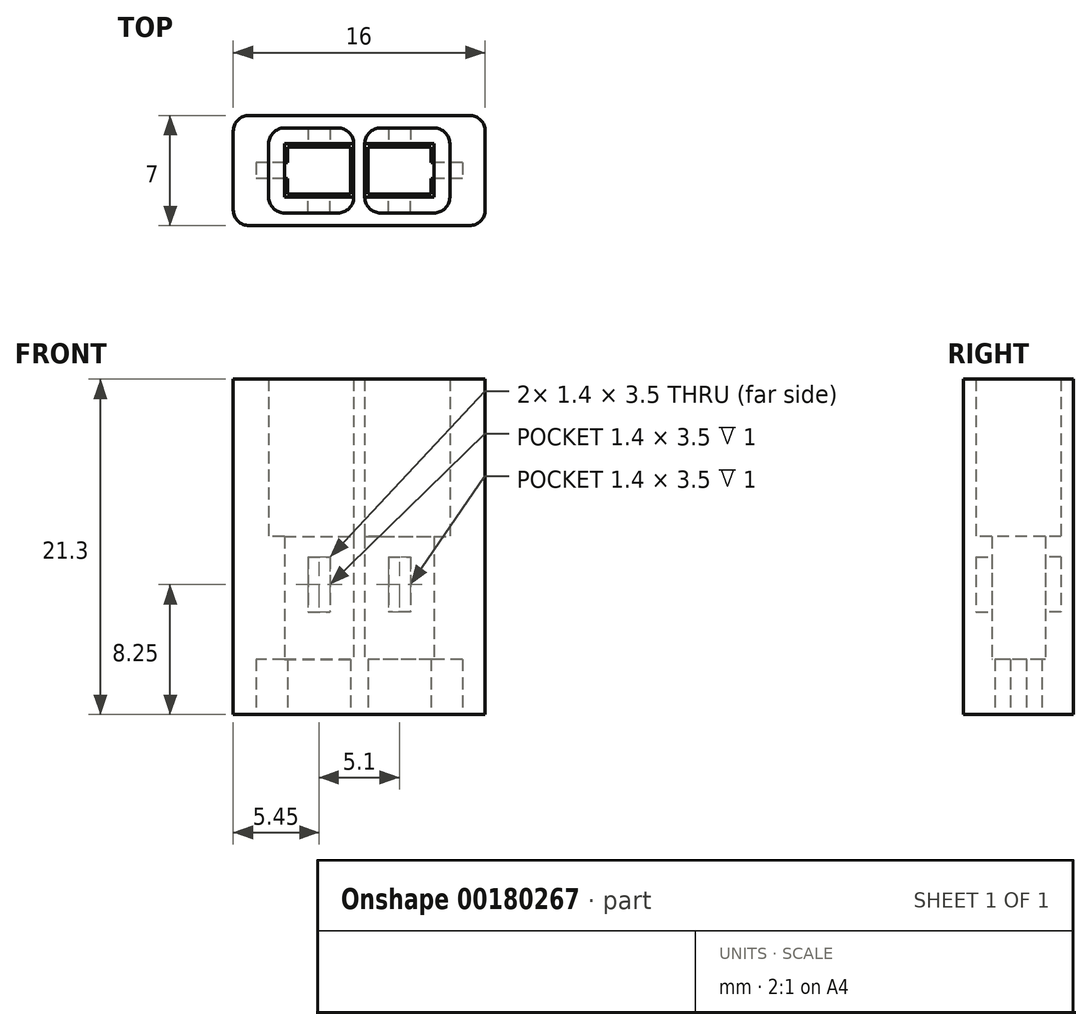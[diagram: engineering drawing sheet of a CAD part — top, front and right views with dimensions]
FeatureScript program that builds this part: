
annotation { "Feature Type Name" : "Feature", "Feature Type Description" : "" }
export const myFeature = defineFeature(function(context is Context, id is Id, definition is map)
    precondition{}
    {
        {
            var Q0;
            Q0=qCreatedBy(makeId("Top.planeOp"),FACE);
            var sketch = newSketch(context, id + "F0", { "sketchPlane" : qUnion([Q0])});
            skLineSegment(sketch, "E0.bottom", {"start": v(-37.92, 21.45) * mm, "end": v(-21.92, 21.45) * mm});
            skLineSegment(sketch, "E0.top", {"start": v(-37.92, 14.45) * mm, "end": v(-21.92, 14.45) * mm});
            skLineSegment(sketch, "E0.left", {"start": v(-37.92, 21.45) * mm, "end": v(-37.92, 14.45) * mm});
            skLineSegment(sketch, "E0.right", {"start": v(-21.92, 21.45) * mm, "end": v(-21.92, 14.45) * mm});
            skLineSegment(sketch, "E1.0", {"start": v(-30.47, 19.45) * mm, "end": v(-30.47, 16.45) * mm});
            skLineSegment(sketch, "E2.MirrorCS", {"start": v(-29.37, 19.45) * mm, "end": v(-29.37, 16.45) * mm});
            skLineSegment(sketch, "E3.0", {"start": v(-25.37, 19.45) * mm, "end": v(-29.37, 19.45) * mm});
            skLineSegment(sketch, "E4.MirrorCS", {"start": v(-25.37, 16.45) * mm, "end": v(-29.37, 16.45) * mm});
            skLineSegment(sketch, "E5", {"start": v(-29.37, 21.45) * mm, "end": v(-25.37, 21.45) * mm});
            skLineSegment(sketch, "E6", {"start": v(-25.37, 19.45) * mm, "end": v(-25.37, 18.45) * mm});
            skLineSegment(sketch, "E7.MirrorCS", {"start": v(-34.47, 19.45) * mm, "end": v(-34.47, 18.45) * mm});
            skPoint(sketch, "E8.orphan", {"position": v(-37.92, 19.45) * mm});
            skPoint(sketch, "E9.orphan", {"position": v(-34.47, 21.45) * mm});
            skPoint(sketch, "E10.orphan", {"position": v(-37.92, 16.45) * mm});
            skPoint(sketch, "E11.orphan", {"position": v(-34.47, 14.45) * mm});
            skPoint(sketch, "E12.orphan", {"position": v(-29.37, 14.45) * mm});
            skPoint(sketch, "E13.orphan", {"position": v(-29.92, 14.45) * mm});
            skPoint(sketch, "E14.orphan", {"position": v(-30.47, 14.45) * mm});
            skPoint(sketch, "E15.orphan", {"position": v(-25.37, 14.45) * mm});
            skPoint(sketch, "E16.orphan", {"position": v(-21.92, 16.45) * mm});
            skPoint(sketch, "E17.orphan", {"position": v(-21.92, 19.45) * mm});
            skPoint(sketch, "E18.orphan", {"position": v(-29.92, 21.45) * mm});
            skPoint(sketch, "E19.orphan", {"position": v(-30.47, 21.45) * mm});
            skLineSegment(sketch, "E20.trimOffspring", {"start": v(-30.47, 19.45) * mm, "end": v(-34.47, 19.45) * mm});
            skLineSegment(sketch, "E21.trimOffspring", {"start": v(-30.47, 16.45) * mm, "end": v(-34.47, 16.45) * mm});
            skLineSegment(sketch, "E22.0", {"start": v(-34.47, 18.45) * mm, "end": v(-36.47, 18.45) * mm});
            skLineSegment(sketch, "E23.MirrorCS", {"start": v(-34.47, 17.45) * mm, "end": v(-36.47, 17.45) * mm});
            skLineSegment(sketch, "E24.0", {"start": v(-23.37, 18.45) * mm, "end": v(-25.37, 18.45) * mm});
            skLineSegment(sketch, "E25.MirrorCS", {"start": v(-23.37, 17.45) * mm, "end": v(-25.37, 17.45) * mm});
            skLineSegment(sketch, "E26", {"start": v(-25.37, 21.45) * mm, "end": v(-23.37, 21.45) * mm});
            skLineSegment(sketch, "E27", {"start": v(-23.37, 18.45) * mm, "end": v(-23.37, 17.45) * mm});
            skLineSegment(sketch, "E28", {"start": v(-29.92, 21.45) * mm, "end": v(-29.92, 14.45) * mm});
            skLineSegment(sketch, "E29.MirrorCS", {"start": v(-36.47, 18.45) * mm, "end": v(-36.47, 17.45) * mm});
            skPoint(sketch, "E30.orphan", {"position": v(-37.92, 17.95) * mm});
            skPoint(sketch, "E31.orphan", {"position": v(-37.92, 18.45) * mm});
            skPoint(sketch, "E32.orphan", {"position": v(-37.92, 17.45) * mm});
            skPoint(sketch, "E33.orphan", {"position": v(-36.47, 21.45) * mm});
            skPoint(sketch, "E34.orphan", {"position": v(-36.47, 14.45) * mm});
            skLineSegment(sketch, "E35.trimOffspring", {"start": v(-34.47, 17.45) * mm, "end": v(-34.47, 16.45) * mm});
            skPoint(sketch, "E36.orphan", {"position": v(-23.37, 14.45) * mm});
            skPoint(sketch, "E37.orphan", {"position": v(-21.92, 17.45) * mm});
            skPoint(sketch, "E38.orphan", {"position": v(-21.92, 17.95) * mm});
            skPoint(sketch, "E39.orphan", {"position": v(-21.92, 18.45) * mm});
            skLineSegment(sketch, "E40.trimOffspring", {"start": v(-25.37, 17.45) * mm, "end": v(-25.37, 16.45) * mm});
            skSolve(sketch);
        }
        {
            var Q0;
            Q0 = qSketchRegion(id + "F0", true);
            extrude(context, id + "F1", {"entities" : qUnion([Q0]), "depth" : 3.5 * mm});
        }
        {
            var Q0;
            Q0=makeQuery(id+"F1.opExtrude","CAP_FACE",FACE,{"disambiguationData":[OSD([sQuery(id+"F0.wireOp",EDGE,"E0.bottom"),sQuery(id+"F0.wireOp",EDGE,"E0.top"),sQuery(id+"F0.wireOp",EDGE,"E0.left"),sQuery(id+"F0.wireOp",EDGE,"E0.right"),sQuery(id+"F0.wireOp",EDGE,"E1.0"),sQuery(id+"F0.wireOp",EDGE,"E2.MirrorCS"),sQuery(id+"F0.wireOp",EDGE,"E3.0"),sQuery(id+"F0.wireOp",EDGE,"E4.MirrorCS"),sQuery(id+"F0.wireOp",EDGE,"E5"),sQuery(id+"F0.wireOp",EDGE,"E6"),sQuery(id+"F0.wireOp",EDGE,"E7.MirrorCS"),sQuery(id+"F0.wireOp",EDGE,"E20.trimOffspring"),sQuery(id+"F0.wireOp",EDGE,"E21.trimOffspring"),sQuery(id+"F0.wireOp",EDGE,"E22.0"),sQuery(id+"F0.wireOp",EDGE,"E23.MirrorCS"),sQuery(id+"F0.wireOp",EDGE,"E24.0"),sQuery(id+"F0.wireOp",EDGE,"E25.MirrorCS"),sQuery(id+"F0.wireOp",EDGE,"E26"),sQuery(id+"F0.wireOp",EDGE,"E27"),sQuery(id+"F0.wireOp",EDGE,"E29.MirrorCS"),sQuery(id+"F0.wireOp",EDGE,"E35.trimOffspring"),sQuery(id+"F0.wireOp",EDGE,"E40.trimOffspring")])],"isStart":false});
            var sketch = newSketch(context, id + "F2", { "sketchPlane" : qUnion([Q0])});
            skLineSegment(sketch, "E41.0", {"start": v(-30.47, 19.45) * mm, "end": v(-34.47, 19.45) * mm});
            skLineSegment(sketch, "E42.0", {"start": v(-30.47, 19.45) * mm, "end": v(-30.47, 16.45) * mm});
            skLineSegment(sketch, "E43.0", {"start": v(-30.47, 16.45) * mm, "end": v(-34.47, 16.45) * mm});
            skLineSegment(sketch, "E44.bottom", {"start": v(-34.47, 19.45) * mm, "end": v(-30.47, 19.45) * mm});
            skLineSegment(sketch, "E44.top", {"start": v(-34.47, 16.45) * mm, "end": v(-30.47, 16.45) * mm});
            skLineSegment(sketch, "E44.left", {"start": v(-34.47, 19.45) * mm, "end": v(-34.47, 16.45) * mm});
            skLineSegment(sketch, "E45.0", {"start": v(-37.92, 21.45) * mm, "end": v(-21.92, 21.45) * mm});
            skLineSegment(sketch, "E46.0", {"start": v(-34.67, 19.65) * mm, "end": v(-30.27, 19.65) * mm});
            skLineSegment(sketch, "E46.1", {"start": v(-34.67, 19.65) * mm, "end": v(-34.67, 16.25) * mm});
            skLineSegment(sketch, "E46.2", {"start": v(-34.67, 16.25) * mm, "end": v(-30.27, 16.25) * mm});
            skLineSegment(sketch, "E46.3", {"start": v(-30.27, 19.65) * mm, "end": v(-30.27, 16.25) * mm});
            skLineSegment(sketch, "E47", {"start": v(-29.92, 21.45) * mm, "end": v(-29.92, 14.45) * mm});
            skLineSegment(sketch, "E48.MirrorCS", {"start": v(-25.17, 19.65) * mm, "end": v(-29.57, 19.65) * mm});
            skLineSegment(sketch, "E49.MirrorCS", {"start": v(-29.57, 19.65) * mm, "end": v(-29.57, 16.25) * mm});
            skLineSegment(sketch, "E50.MirrorCS", {"start": v(-25.17, 16.25) * mm, "end": v(-29.57, 16.25) * mm});
            skLineSegment(sketch, "E51.MirrorCS", {"start": v(-25.17, 19.65) * mm, "end": v(-25.17, 16.25) * mm});
            skLineSegment(sketch, "E52.0", {"start": v(-37.92, 21.45) * mm, "end": v(-37.92, 14.45) * mm});
            skLineSegment(sketch, "E53.0", {"start": v(-37.92, 14.45) * mm, "end": v(-21.92, 14.45) * mm});
            skLineSegment(sketch, "E54.0", {"start": v(-21.92, 21.45) * mm, "end": v(-21.92, 14.45) * mm});
            skSolve(sketch);
        }
        {
            var Q0;
            Q0 = qSketchRegion(id + "F2", true);
            extrude(context, id + "F3", {"entities" : qUnion([Q0]), "operationType" : NewBodyOperationType.ADD, "depth" : 3 * mm});
        }
        {
            var Q0;
            Q0=makeQuery(id+"F3.opExtrude","CAP_FACE",FACE,{"disambiguationData":[OSD([sQuery(id+"F2.wireOp",EDGE,"E45.0"),sQuery(id+"F2.wireOp",EDGE,"E46.0"),sQuery(id+"F2.wireOp",EDGE,"E46.1"),sQuery(id+"F2.wireOp",EDGE,"E46.2"),sQuery(id+"F2.wireOp",EDGE,"E46.3"),sQuery(id+"F2.wireOp",EDGE,"E48.MirrorCS"),sQuery(id+"F2.wireOp",EDGE,"E49.MirrorCS"),sQuery(id+"F2.wireOp",EDGE,"E50.MirrorCS"),sQuery(id+"F2.wireOp",EDGE,"E51.MirrorCS"),sQuery(id+"F2.wireOp",EDGE,"E52.0"),sQuery(id+"F2.wireOp",EDGE,"E53.0"),sQuery(id+"F2.wireOp",EDGE,"E54.0")])],"isStart":false});
            var sketch = newSketch(context, id + "F4", { "sketchPlane" : qUnion([Q0])});
            skLineSegment(sketch, "E55.0", {"start": v(-34.67, 19.65) * mm, "end": v(-30.27, 19.65) * mm});
            skLineSegment(sketch, "E56.0", {"start": v(-34.67, 16.25) * mm, "end": v(-30.27, 16.25) * mm});
            skLineSegment(sketch, "E57.0", {"start": v(-30.27, 19.65) * mm, "end": v(-30.27, 16.25) * mm});
            skLineSegment(sketch, "E58.0", {"start": v(-34.67, 19.65) * mm, "end": v(-34.67, 16.25) * mm});
            skLineSegment(sketch, "E59", {"start": v(-29.92, 21.45) * mm, "end": v(-29.92, 14.45) * mm});
            skLineSegment(sketch, "E60", {"start": v(-34.67, 17.95) * mm, "end": v(-30.27, 17.95) * mm});
            skLineSegment(sketch, "E61", {"start": v(-32.47, 19.65) * mm, "end": v(-32.47, 20.65) * mm});
            skLineSegment(sketch, "E62", {"start": v(-32.47, 20.65) * mm, "end": v(-31.77, 20.65) * mm});
            skLineSegment(sketch, "E63", {"start": v(-32.47, 20.65) * mm, "end": v(-33.17, 20.65) * mm});
            skLineSegment(sketch, "E64", {"start": v(-31.77, 20.65) * mm, "end": v(-31.77, 19.65) * mm});
            skLineSegment(sketch, "E65", {"start": v(-33.17, 20.65) * mm, "end": v(-33.17, 19.65) * mm});
            skLineSegment(sketch, "E66.MirrorCS", {"start": v(-31.77, 15.25) * mm, "end": v(-31.77, 16.25) * mm});
            skLineSegment(sketch, "E67.MirrorCS", {"start": v(-32.47, 15.25) * mm, "end": v(-31.77, 15.25) * mm});
            skLineSegment(sketch, "E68.MirrorCS", {"start": v(-32.47, 15.25) * mm, "end": v(-33.17, 15.25) * mm});
            skLineSegment(sketch, "E69.MirrorCS", {"start": v(-33.17, 15.25) * mm, "end": v(-33.17, 16.25) * mm});
            skLineSegment(sketch, "E70.MirrorCS", {"start": v(-28.07, 20.65) * mm, "end": v(-28.07, 19.65) * mm});
            skLineSegment(sketch, "E71.MirrorCS", {"start": v(-27.37, 20.65) * mm, "end": v(-28.07, 20.65) * mm});
            skLineSegment(sketch, "E72.MirrorCS", {"start": v(-26.67, 20.65) * mm, "end": v(-26.67, 19.65) * mm});
            skLineSegment(sketch, "E73.MirrorCS", {"start": v(-27.37, 20.65) * mm, "end": v(-26.67, 20.65) * mm});
            skLineSegment(sketch, "E74.MirrorCS", {"start": v(-26.67, 15.25) * mm, "end": v(-26.67, 16.25) * mm});
            skLineSegment(sketch, "E75.MirrorCS", {"start": v(-27.37, 15.25) * mm, "end": v(-26.67, 15.25) * mm});
            skLineSegment(sketch, "E76.MirrorCS", {"start": v(-27.37, 15.25) * mm, "end": v(-28.07, 15.25) * mm});
            skLineSegment(sketch, "E77.MirrorCS", {"start": v(-28.07, 15.25) * mm, "end": v(-28.07, 16.25) * mm});
            skLineSegment(sketch, "E78.0", {"start": v(-25.17, 19.65) * mm, "end": v(-29.57, 19.65) * mm});
            skLineSegment(sketch, "E79.0", {"start": v(-25.17, 19.65) * mm, "end": v(-25.17, 16.25) * mm});
            skLineSegment(sketch, "E80.0", {"start": v(-25.17, 16.25) * mm, "end": v(-29.57, 16.25) * mm});
            skLineSegment(sketch, "E81.0", {"start": v(-29.57, 19.65) * mm, "end": v(-29.57, 16.25) * mm});
            skLineSegment(sketch, "E82.0", {"start": v(-37.92, 21.45) * mm, "end": v(-21.92, 21.45) * mm});
            skLineSegment(sketch, "E83.0", {"start": v(-21.92, 21.45) * mm, "end": v(-21.92, 14.45) * mm});
            skLineSegment(sketch, "E84.0", {"start": v(-37.92, 14.45) * mm, "end": v(-21.92, 14.45) * mm});
            skLineSegment(sketch, "E85.0", {"start": v(-37.92, 21.45) * mm, "end": v(-37.92, 14.45) * mm});
            skSolve(sketch);
        }
        {
            var Q0;
            Q0 = qSketchRegion(id + "F4", true);
            extrude(context, id + "F5", {"entities" : qUnion([Q0]), "operationType" : NewBodyOperationType.ADD, "depth" : 3.5 * mm});
        }
        {
            var Q0;
            Q0=makeQuery(id+"F5.opExtrude","CAP_FACE",FACE,{"disambiguationData":[OSD([sQuery(id+"F4.wireOp",EDGE,"E55.0"),sQuery(id+"F4.wireOp",EDGE,"E56.0"),sQuery(id+"F4.wireOp",EDGE,"E57.0"),sQuery(id+"F4.wireOp",EDGE,"E58.0"),sQuery(id+"F4.wireOp",EDGE,"E62"),sQuery(id+"F4.wireOp",EDGE,"E63"),sQuery(id+"F4.wireOp",EDGE,"E64"),sQuery(id+"F4.wireOp",EDGE,"E65"),sQuery(id+"F4.wireOp",EDGE,"E66.MirrorCS"),sQuery(id+"F4.wireOp",EDGE,"E67.MirrorCS"),sQuery(id+"F4.wireOp",EDGE,"E68.MirrorCS"),sQuery(id+"F4.wireOp",EDGE,"E69.MirrorCS"),sQuery(id+"F4.wireOp",EDGE,"E70.MirrorCS"),sQuery(id+"F4.wireOp",EDGE,"E71.MirrorCS"),sQuery(id+"F4.wireOp",EDGE,"E72.MirrorCS"),sQuery(id+"F4.wireOp",EDGE,"E73.MirrorCS"),sQuery(id+"F4.wireOp",EDGE,"E74.MirrorCS"),sQuery(id+"F4.wireOp",EDGE,"E75.MirrorCS"),sQuery(id+"F4.wireOp",EDGE,"E76.MirrorCS"),sQuery(id+"F4.wireOp",EDGE,"E77.MirrorCS"),sQuery(id+"F4.wireOp",EDGE,"E78.0"),sQuery(id+"F4.wireOp",EDGE,"E79.0"),sQuery(id+"F4.wireOp",EDGE,"E80.0"),sQuery(id+"F4.wireOp",EDGE,"E81.0"),sQuery(id+"F4.wireOp",EDGE,"E82.0"),sQuery(id+"F4.wireOp",EDGE,"E83.0"),sQuery(id+"F4.wireOp",EDGE,"E84.0"),sQuery(id+"F4.wireOp",EDGE,"E85.0")])],"isStart":false});
            var sketch = newSketch(context, id + "F6", { "sketchPlane" : qUnion([Q0])});
            skLineSegment(sketch, "E86.0", {"start": v(-37.92, 21.45) * mm, "end": v(-21.92, 21.45) * mm});
            skLineSegment(sketch, "E87.0", {"start": v(-21.92, 21.45) * mm, "end": v(-21.92, 14.45) * mm});
            skLineSegment(sketch, "E88.0", {"start": v(-37.92, 14.45) * mm, "end": v(-21.92, 14.45) * mm});
            skLineSegment(sketch, "E89.0", {"start": v(-37.92, 21.45) * mm, "end": v(-37.92, 14.45) * mm});
            skLineSegment(sketch, "E90.bottom", {"start": v(-34.67, 19.65) * mm, "end": v(-30.27, 19.65) * mm});
            skLineSegment(sketch, "E90.top", {"start": v(-34.67, 16.25) * mm, "end": v(-30.27, 16.25) * mm});
            skLineSegment(sketch, "E90.left", {"start": v(-34.67, 19.65) * mm, "end": v(-34.67, 16.25) * mm});
            skLineSegment(sketch, "E90.right", {"start": v(-30.27, 19.65) * mm, "end": v(-30.27, 16.25) * mm});
            skLineSegment(sketch, "E91.bottom", {"start": v(-29.57, 19.65) * mm, "end": v(-25.17, 19.65) * mm});
            skLineSegment(sketch, "E91.top", {"start": v(-29.57, 16.25) * mm, "end": v(-25.17, 16.25) * mm});
            skLineSegment(sketch, "E91.left", {"start": v(-29.57, 19.65) * mm, "end": v(-29.57, 16.25) * mm});
            skLineSegment(sketch, "E91.right", {"start": v(-25.17, 19.65) * mm, "end": v(-25.17, 16.25) * mm});
            skSolve(sketch);
        }
        {
            var Q0;
            Q0 = qSketchRegion(id + "F6", true);
            extrude(context, id + "F7", {"entities" : qUnion([Q0]), "operationType" : NewBodyOperationType.ADD, "depth" : 1.3 * mm});
        }
        {
            var Q0;
            Q0=makeQuery(id+"F7.opExtrude","CAP_FACE",FACE,{"disambiguationData":[OSD([sQuery(id+"F6.wireOp",EDGE,"E86.0"),sQuery(id+"F6.wireOp",EDGE,"E87.0"),sQuery(id+"F6.wireOp",EDGE,"E88.0"),sQuery(id+"F6.wireOp",EDGE,"E89.0"),sQuery(id+"F6.wireOp",EDGE,"E90.bottom"),sQuery(id+"F6.wireOp",EDGE,"E90.top"),sQuery(id+"F6.wireOp",EDGE,"E90.left"),sQuery(id+"F6.wireOp",EDGE,"E90.right"),sQuery(id+"F6.wireOp",EDGE,"E91.bottom"),sQuery(id+"F6.wireOp",EDGE,"E91.top"),sQuery(id+"F6.wireOp",EDGE,"E91.left"),sQuery(id+"F6.wireOp",EDGE,"E91.right")])],"isStart":false});
            var sketch = newSketch(context, id + "F8", { "sketchPlane" : qUnion([Q0])});
            skLineSegment(sketch, "E92.bottom", {"start": v(-34.67, 19.65) * mm, "end": v(-30.27, 19.65) * mm});
            skLineSegment(sketch, "E92.top", {"start": v(-34.67, 16.25) * mm, "end": v(-30.27, 16.25) * mm});
            skLineSegment(sketch, "E92.left", {"start": v(-34.67, 19.65) * mm, "end": v(-34.67, 16.25) * mm});
            skLineSegment(sketch, "E92.right", {"start": v(-30.27, 19.65) * mm, "end": v(-30.27, 16.25) * mm});
            skLineSegment(sketch, "E93.bottom", {"start": v(-29.57, 16.25) * mm, "end": v(-25.17, 16.25) * mm});
            skLineSegment(sketch, "E93.top", {"start": v(-29.57, 19.65) * mm, "end": v(-25.17, 19.65) * mm});
            skLineSegment(sketch, "E93.left", {"start": v(-29.57, 16.25) * mm, "end": v(-29.57, 19.65) * mm});
            skLineSegment(sketch, "E93.right", {"start": v(-25.17, 16.25) * mm, "end": v(-25.17, 19.65) * mm});
            skLineSegment(sketch, "E94.0", {"start": v(-35.67, 20.65) * mm, "end": v(-30.27, 20.65) * mm});
            skLineSegment(sketch, "E94.1", {"start": v(-35.67, 20.65) * mm, "end": v(-35.67, 15.25) * mm});
            skLineSegment(sketch, "E94.2", {"start": v(-35.67, 15.25) * mm, "end": v(-30.27, 15.25) * mm});
            skLineSegment(sketch, "E95.0", {"start": v(-29.57, 20.65) * mm, "end": v(-24.17, 20.65) * mm});
            skLineSegment(sketch, "E95.1", {"start": v(-24.17, 15.25) * mm, "end": v(-24.17, 20.65) * mm});
            skLineSegment(sketch, "E95.2", {"start": v(-29.57, 15.25) * mm, "end": v(-24.17, 15.25) * mm});
            skLineSegment(sketch, "E96", {"start": v(-30.27, 20.65) * mm, "end": v(-30.27, 15.25) * mm});
            skLineSegment(sketch, "E97", {"start": v(-29.57, 20.65) * mm, "end": v(-29.57, 15.25) * mm});
            skSolve(sketch);
        }
        {
            var Q0;
            {var subQ7=sQuery(id+"F8.wireOp",EDGE,"E94.0");Q0=makeQuery(id+"F8.imprint","IMPRINT",FACE,{"disambiguationData":[TD([[makeQuery(id+"F8.imprint","IMPRINT",EDGE,{"derivedFrom":subQ7}),1.0]])]});}
            extrude(context, id + "F9", {"entities" : qUnion([Q0]), "operationType" : NewBodyOperationType.ADD, "depth" : 10 * mm});
        }
        {
            var Q0;
            {var subQ0=sQuery(id+"F6.wireOp",EDGE,"E89.0");var subQ1=sQuery(id+"F6.wireOp",EDGE,"E88.0");Q0=makeQuery(id+"F9.boolean.opBoolean","MERGE",EDGE,{"derivedFrom":[makeQuery(id+"F7.boolean.opBoolean","MERGE",EDGE,{"derivedFrom":[makeQuery(id+"F5.boolean.opBoolean","MERGE",EDGE,{"derivedFrom":[makeQuery(id+"F3.boolean.opBoolean","MERGE",EDGE,{"derivedFrom":[makeQuery(id+"F1.opExtrude","SWEPT_EDGE",EDGE,{"disambiguationData":[OSD([sQuery(id+"F0.wireOp",EDGE,"E0.top"),sQuery(id+"F0.wireOp",EDGE,"E0.left")])]}),makeQuery(id+"F3.opExtrude","SWEPT_EDGE",EDGE,{"disambiguationData":[OSD([sQuery(id+"F2.wireOp",EDGE,"E52.0"),sQuery(id+"F2.wireOp",EDGE,"E53.0")])]})]}),makeQuery(id+"F5.opExtrude","SWEPT_EDGE",EDGE,{"disambiguationData":[OSD([sQuery(id+"F4.wireOp",EDGE,"E84.0"),sQuery(id+"F4.wireOp",EDGE,"E85.0")])]})]}),makeQuery(id+"F7.opExtrude","SWEPT_EDGE",EDGE,{"disambiguationData":[OSD([subQ1,subQ0])]})]}),makeQuery(id+"F9.opExtrude","SWEPT_EDGE",EDGE,{"disambiguationData":[OSD([subQ1,subQ0])]})]});}
            var Q1;
            {var subQ0=sQuery(id+"F6.wireOp",EDGE,"E88.0");var subQ1=sQuery(id+"F6.wireOp",EDGE,"E87.0");Q1=makeQuery(id+"F9.boolean.opBoolean","MERGE",EDGE,{"derivedFrom":[makeQuery(id+"F7.boolean.opBoolean","MERGE",EDGE,{"derivedFrom":[makeQuery(id+"F5.boolean.opBoolean","MERGE",EDGE,{"derivedFrom":[makeQuery(id+"F3.boolean.opBoolean","MERGE",EDGE,{"derivedFrom":[makeQuery(id+"F1.opExtrude","SWEPT_EDGE",EDGE,{"disambiguationData":[OSD([sQuery(id+"F0.wireOp",EDGE,"E0.top"),sQuery(id+"F0.wireOp",EDGE,"E0.right")])]}),makeQuery(id+"F3.opExtrude","SWEPT_EDGE",EDGE,{"disambiguationData":[OSD([sQuery(id+"F2.wireOp",EDGE,"E53.0"),sQuery(id+"F2.wireOp",EDGE,"E54.0")])]})]}),makeQuery(id+"F5.opExtrude","SWEPT_EDGE",EDGE,{"disambiguationData":[OSD([sQuery(id+"F4.wireOp",EDGE,"E83.0"),sQuery(id+"F4.wireOp",EDGE,"E84.0")])]})]}),makeQuery(id+"F7.opExtrude","SWEPT_EDGE",EDGE,{"disambiguationData":[OSD([subQ1,subQ0])]})]}),makeQuery(id+"F9.opExtrude","SWEPT_EDGE",EDGE,{"disambiguationData":[OSD([subQ1,subQ0])]})]});}
            var Q2;
            {var subQ0=sQuery(id+"F6.wireOp",EDGE,"E89.0");var subQ1=sQuery(id+"F6.wireOp",EDGE,"E86.0");Q2=makeQuery(id+"F9.boolean.opBoolean","MERGE",EDGE,{"derivedFrom":[makeQuery(id+"F7.boolean.opBoolean","MERGE",EDGE,{"derivedFrom":[makeQuery(id+"F5.boolean.opBoolean","MERGE",EDGE,{"derivedFrom":[makeQuery(id+"F3.boolean.opBoolean","MERGE",EDGE,{"derivedFrom":[makeQuery(id+"F1.opExtrude","SWEPT_EDGE",EDGE,{"disambiguationData":[OSD([sQuery(id+"F0.wireOp",EDGE,"E0.bottom"),sQuery(id+"F0.wireOp",EDGE,"E0.left")])]}),makeQuery(id+"F3.opExtrude","SWEPT_EDGE",EDGE,{"disambiguationData":[OSD([sQuery(id+"F2.wireOp",EDGE,"E45.0"),sQuery(id+"F2.wireOp",EDGE,"E52.0")])]})]}),makeQuery(id+"F5.opExtrude","SWEPT_EDGE",EDGE,{"disambiguationData":[OSD([sQuery(id+"F4.wireOp",EDGE,"E82.0"),sQuery(id+"F4.wireOp",EDGE,"E85.0")])]})]}),makeQuery(id+"F7.opExtrude","SWEPT_EDGE",EDGE,{"disambiguationData":[OSD([subQ1,subQ0])]})]}),makeQuery(id+"F9.opExtrude","SWEPT_EDGE",EDGE,{"disambiguationData":[OSD([subQ1,subQ0])]})]});}
            var Q3;
            {var subQ0=sQuery(id+"F6.wireOp",EDGE,"E87.0");var subQ1=sQuery(id+"F6.wireOp",EDGE,"E86.0");Q3=makeQuery(id+"F9.boolean.opBoolean","MERGE",EDGE,{"derivedFrom":[makeQuery(id+"F7.boolean.opBoolean","MERGE",EDGE,{"derivedFrom":[makeQuery(id+"F5.boolean.opBoolean","MERGE",EDGE,{"derivedFrom":[makeQuery(id+"F3.boolean.opBoolean","MERGE",EDGE,{"derivedFrom":[makeQuery(id+"F1.opExtrude","SWEPT_EDGE",EDGE,{"disambiguationData":[OSD([sQuery(id+"F0.wireOp",EDGE,"E0.bottom"),sQuery(id+"F0.wireOp",EDGE,"E0.right")])]}),makeQuery(id+"F3.opExtrude","SWEPT_EDGE",EDGE,{"disambiguationData":[OSD([sQuery(id+"F2.wireOp",EDGE,"E45.0"),sQuery(id+"F2.wireOp",EDGE,"E54.0")])]})]}),makeQuery(id+"F5.opExtrude","SWEPT_EDGE",EDGE,{"disambiguationData":[OSD([sQuery(id+"F4.wireOp",EDGE,"E82.0"),sQuery(id+"F4.wireOp",EDGE,"E83.0")])]})]}),makeQuery(id+"F7.opExtrude","SWEPT_EDGE",EDGE,{"disambiguationData":[OSD([subQ1,subQ0])]})]}),makeQuery(id+"F9.opExtrude","SWEPT_EDGE",EDGE,{"disambiguationData":[OSD([subQ1,subQ0])]})]});}
            fillet(context, id + "F10", {"entities" : qUnion([Q0, Q1, Q2, Q3]), "radius" : 1 * mm, "tangentPropagation" : true, "allowEdgeOverflow" : false});
        }
        {
            var Q0;
            Q0=makeQuery(id+"F9.opExtrude","SWEPT_EDGE",EDGE,{"disambiguationData":[OSD([sQuery(id+"F8.wireOp",EDGE,"E95.1"),sQuery(id+"F8.wireOp",EDGE,"E95.2")])]});
            var Q1;
            Q1=makeQuery(id+"F9.opExtrude","SWEPT_EDGE",EDGE,{"disambiguationData":[OSD([sQuery(id+"F8.wireOp",EDGE,"E94.2"),sQuery(id+"F8.wireOp",EDGE,"E96")])]});
            var Q2;
            Q2=makeQuery(id+"F9.opExtrude","SWEPT_EDGE",EDGE,{"disambiguationData":[OSD([sQuery(id+"F8.wireOp",EDGE,"E94.1"),sQuery(id+"F8.wireOp",EDGE,"E94.2")])]});
            var Q3;
            Q3=makeQuery(id+"F9.opExtrude","SWEPT_EDGE",EDGE,{"disambiguationData":[OSD([sQuery(id+"F8.wireOp",EDGE,"E95.2"),sQuery(id+"F8.wireOp",EDGE,"E97")])]});
            var Q4;
            Q4=makeQuery(id+"F9.opExtrude","SWEPT_EDGE",EDGE,{"disambiguationData":[OSD([sQuery(id+"F8.wireOp",EDGE,"E95.0"),sQuery(id+"F8.wireOp",EDGE,"E95.1")])]});
            var Q5;
            Q5=makeQuery(id+"F9.opExtrude","SWEPT_EDGE",EDGE,{"disambiguationData":[OSD([sQuery(id+"F8.wireOp",EDGE,"E94.0"),sQuery(id+"F8.wireOp",EDGE,"E96")])]});
            var Q6;
            Q6=makeQuery(id+"F9.opExtrude","SWEPT_EDGE",EDGE,{"disambiguationData":[OSD([sQuery(id+"F8.wireOp",EDGE,"E95.0"),sQuery(id+"F8.wireOp",EDGE,"E97")])]});
            var Q7;
            Q7=makeQuery(id+"F9.opExtrude","SWEPT_EDGE",EDGE,{"disambiguationData":[OSD([sQuery(id+"F8.wireOp",EDGE,"E94.0"),sQuery(id+"F8.wireOp",EDGE,"E94.1")])]});
            fillet(context, id + "F11", {"entities" : qUnion([Q0, Q1, Q2, Q3, Q4, Q5, Q6, Q7]), "radius" : 1 * mm, "tangentPropagation" : true, "allowEdgeOverflow" : false});
        }
    });
